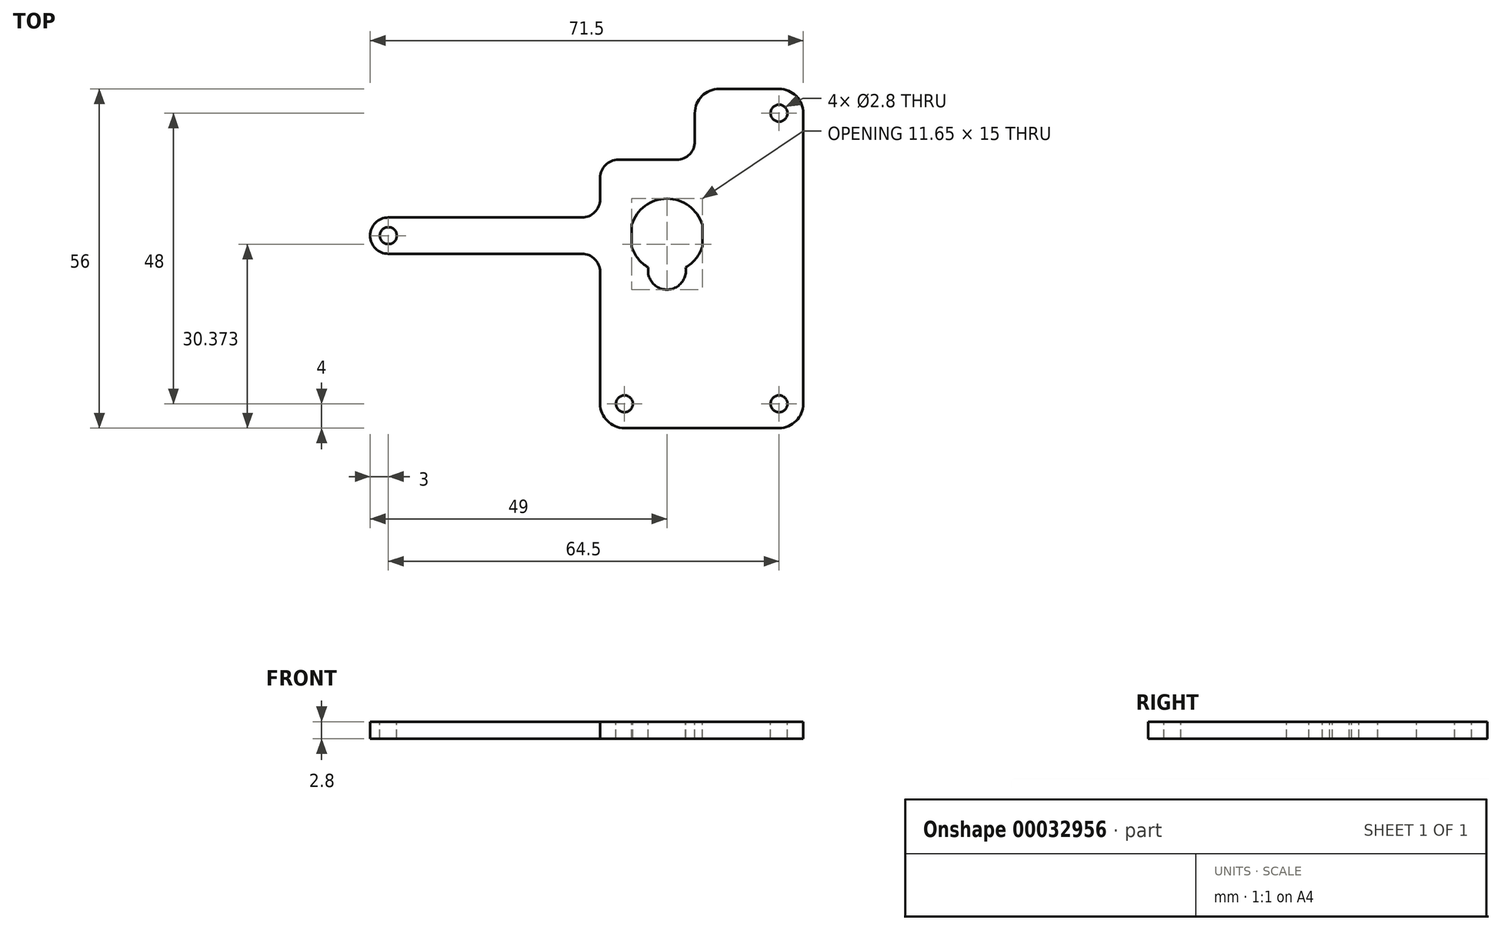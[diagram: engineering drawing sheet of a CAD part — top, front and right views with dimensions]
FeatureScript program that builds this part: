
annotation { "Feature Type Name" : "Feature", "Feature Type Description" : "" }
export const myFeature = defineFeature(function(context is Context, id is Id, definition is map)
    precondition{}
    {
        {
            var Q0;
            Q0=qCreatedBy(makeId("Top.planeOp"),FACE);
            var sketch = newSketch(context, id + "F0", { "sketchPlane" : qUnion([Q0])});
            skLineSegment(sketch, "E0.rect.bottom", {"start": v(5.82, -11.88) * mm, "end": v(-5.83, -11.88) * mm});
            skLineSegment(sketch, "E0.rect.top", {"start": v(5.83, 11.88) * mm, "end": v(-5.82, 11.88) * mm});
            skLineSegment(sketch, "E0.rect.left", {"start": v(5.82, -11.88) * mm, "end": v(5.83, 11.88) * mm});
            skLineSegment(sketch, "E0.rect.right", {"start": v(-5.83, -11.88) * mm, "end": v(-5.82, 11.87) * mm});
            skPoint(sketch, "E0.rect.middle", {"position": v(0, 0) * mm});
            skSolve(sketch);
        }
        {
            var Q0;
            Q0=qSketchRegion(id+"F0",true);
            extrude(context, id + "F1", {"entities" : qUnion([Q0]), "depth" : 20.4 * mm});
        }
        {
            var Q0;
            Q0=makeQuery(id+"F1.opExtrude","CAP_FACE",FACE,{"disambiguationData":[OSD([sQuery(id+"F0.wireOp",EDGE,"E0.rect.bottom"),sQuery(id+"F0.wireOp",EDGE,"E0.rect.top"),sQuery(id+"F0.wireOp",EDGE,"E0.rect.left"),sQuery(id+"F0.wireOp",EDGE,"E0.rect.right")])],"isStart":false});
            var sketch = newSketch(context, id + "F2", { "sketchPlane" : qUnion([Q0])});
            skArc(sketch, "E1", {"start": v(5.83, 7.59) * mm, "mid": v(0, 11.88) * mm, "end": v(-5.83, 7.59) * mm});
            skLineSegment(sketch, "E2", {"start": v(5.83, 7.59) * mm, "end": v(5.83, 3.96) * mm});
            skLineSegment(sketch, "E3.MirrorCS", {"start": v(-5.83, 7.59) * mm, "end": v(-5.83, 3.96) * mm});
            skArc(sketch, "E4.trimOffspring", {"start": v(-5.83, 3.96) * mm, "mid": v(-4.78, 1.98) * mm, "end": v(-3.09, 0.51) * mm});
            skArc(sketch, "E5", {"start": v(-3.09, 0.51) * mm, "mid": v(0, -3.1) * mm, "end": v(3.09, 0.51) * mm});
            skArc(sketch, "E6.trimOffspring", {"start": v(3.09, 0.51) * mm, "mid": v(4.78, 1.98) * mm, "end": v(5.83, 3.96) * mm});
            skSolve(sketch);
        }
        {
            var Q0;
            Q0=qSketchRegion(id+"F2",true);
            extrude(context, id + "F3", {"entities" : qUnion([Q0]), "operationType" : NewBodyOperationType.ADD, "depth" : 6 * mm});
        }
        {
            var Q0;
            {var subQ0=sQuery(id+"F0.wireOp",EDGE,"E0.rect.bottom");var subQ1=sQuery(id+"F0.wireOp",EDGE,"E0.rect.left");var subQ2=sQuery(id+"F0.wireOp",EDGE,"E0.rect.right");Q0=makeQuery(id+"F3.boolean.opBoolean","SPLIT",FACE,{"disambiguationData":[TD([makeQuery(id+"F1.opExtrude","SWEPT_FACE",FACE,{"disambiguationData":[OSD([subQ0])]}),makeQuery(id+"F1.opExtrude","SWEPT_FACE",FACE,{"disambiguationData":[OSD([subQ1])]}),makeQuery(id+"F1.opExtrude","SWEPT_FACE",FACE,{"disambiguationData":[OSD([subQ2])]}),makeQuery(id+"F3.opExtrude","SWEPT_FACE",FACE,{"disambiguationData":[OSD([sQuery(id+"F2.wireOp",EDGE,"E2")])]}),makeQuery(id+"F3.opExtrude","SWEPT_FACE",FACE,{"disambiguationData":[OSD([sQuery(id+"F2.wireOp",EDGE,"E3.MirrorCS")])]}),makeQuery(id+"F3.opExtrude","SWEPT_FACE",FACE,{"disambiguationData":[OSD([sQuery(id+"F2.wireOp",EDGE,"E4.trimOffspring")])]}),makeQuery(id+"F3.opExtrude","SWEPT_FACE",FACE,{"disambiguationData":[OSD([sQuery(id+"F2.wireOp",EDGE,"E5")])]}),makeQuery(id+"F3.opExtrude","SWEPT_FACE",FACE,{"disambiguationData":[OSD([sQuery(id+"F2.wireOp",EDGE,"E6.trimOffspring")])]})])],"derivedFrom":makeQuery(id+"F1.opExtrude","CAP_FACE",FACE,{"disambiguationData":[OSD([subQ0,sQuery(id+"F0.wireOp",EDGE,"E0.rect.top"),subQ1,subQ2])],"isStart":false})});}
            var sketch = newSketch(context, id + "F4", { "sketchPlane" : qUnion([Q0])});
            skLineSegment(sketch, "E7.bottom", {"start": v(-5.83, -11.88) * mm, "end": v(5.82, -11.88) * mm});
            skLineSegment(sketch, "E7.top", {"start": v(-5.83, -16.08) * mm, "end": v(5.82, -16.08) * mm});
            skLineSegment(sketch, "E7.left", {"start": v(-5.83, -11.88) * mm, "end": v(-5.83, -16.08) * mm});
            skLineSegment(sketch, "E7.right", {"start": v(5.82, -11.88) * mm, "end": v(5.82, -16.08) * mm});
            skLineSegment(sketch, "E8.MirrorCS", {"start": v(-5.83, 11.88) * mm, "end": v(-5.83, 16.08) * mm});
            skLineSegment(sketch, "E9.MirrorCS", {"start": v(-5.83, 16.08) * mm, "end": v(5.82, 16.08) * mm});
            skLineSegment(sketch, "E10.MirrorCS", {"start": v(5.82, 11.88) * mm, "end": v(5.82, 16.08) * mm});
            skLineSegment(sketch, "E11.MirrorCS", {"start": v(-5.83, 11.88) * mm, "end": v(5.82, 11.88) * mm});
            skSolve(sketch);
        }
        {
            var Q0;
            Q0=makeQuery(id+"F4.imprint","IMPRINT",FACE,{"disambiguationData":[TD([[makeQuery(id+"F4.imprint","IMPRINT",EDGE,{"derivedFrom":sQuery(id+"F4.wireOp",EDGE,"E7.bottom")}),1.0]])]});
            var Q1;
            Q1=makeQuery(id+"F4.imprint","IMPRINT",FACE,{"disambiguationData":[TD([[makeQuery(id+"F4.imprint","IMPRINT",EDGE,{"derivedFrom":sQuery(id+"F4.wireOp",EDGE,"E8.MirrorCS")}),-1.0]])]});
            extrude(context, id + "F5", {"entities" : qUnion([Q0, Q1]), "operationType" : NewBodyOperationType.ADD, "oppositeDirection" : true, "depth" : 2.8 * mm, "hasSecondDirection" : true, "secondDirectionOppositeDirection" : true, "secondDirectionDepth" : .8 * mm});
        }
        {
            var Q0;
            {var subQ0=sQuery(id+"F0.wireOp",EDGE,"E0.rect.top");var subQ1=sQuery(id+"F0.wireOp",EDGE,"E0.rect.left");Q0=makeQuery(id+"F5.boolean.opBoolean","SPLIT",EDGE,{"disambiguationData":[TD([makeQuery(id+"F1.opExtrude","CAP_FACE",FACE,{"disambiguationData":[OSD([sQuery(id+"F0.wireOp",EDGE,"E0.rect.bottom"),subQ0,subQ1,sQuery(id+"F0.wireOp",EDGE,"E0.rect.right")])],"isStart":true})])],"derivedFrom":makeQuery(id+"F1.opExtrude","SWEPT_EDGE",EDGE,{"disambiguationData":[OSD([subQ0,subQ1])]})});}
            var Q1;
            {var subQ0=sQuery(id+"F0.wireOp",EDGE,"E0.rect.bottom");var subQ1=sQuery(id+"F0.wireOp",EDGE,"E0.rect.left");Q1=makeQuery(id+"F5.boolean.opBoolean","SPLIT",EDGE,{"disambiguationData":[TD([makeQuery(id+"F1.opExtrude","CAP_FACE",FACE,{"disambiguationData":[OSD([subQ0,sQuery(id+"F0.wireOp",EDGE,"E0.rect.top"),subQ1,sQuery(id+"F0.wireOp",EDGE,"E0.rect.right")])],"isStart":true})])],"derivedFrom":makeQuery(id+"F1.opExtrude","SWEPT_EDGE",EDGE,{"disambiguationData":[OSD([subQ0,subQ1])]})});}
            var Q2;
            {var subQ0=sQuery(id+"F0.wireOp",EDGE,"E0.rect.bottom");var subQ1=sQuery(id+"F0.wireOp",EDGE,"E0.rect.right");Q2=makeQuery(id+"F5.boolean.opBoolean","SPLIT",EDGE,{"disambiguationData":[TD([makeQuery(id+"F1.opExtrude","CAP_FACE",FACE,{"disambiguationData":[OSD([subQ0,sQuery(id+"F0.wireOp",EDGE,"E0.rect.top"),sQuery(id+"F0.wireOp",EDGE,"E0.rect.left"),subQ1])],"isStart":true})])],"derivedFrom":makeQuery(id+"F1.opExtrude","SWEPT_EDGE",EDGE,{"disambiguationData":[OSD([subQ0,subQ1])]})});}
            var Q3;
            {var subQ0=sQuery(id+"F0.wireOp",EDGE,"E0.rect.top");var subQ1=sQuery(id+"F0.wireOp",EDGE,"E0.rect.right");Q3=makeQuery(id+"F5.boolean.opBoolean","SPLIT",EDGE,{"disambiguationData":[TD([makeQuery(id+"F1.opExtrude","CAP_FACE",FACE,{"disambiguationData":[OSD([sQuery(id+"F0.wireOp",EDGE,"E0.rect.bottom"),subQ0,sQuery(id+"F0.wireOp",EDGE,"E0.rect.left"),subQ1])],"isStart":true})])],"derivedFrom":makeQuery(id+"F1.opExtrude","SWEPT_EDGE",EDGE,{"disambiguationData":[OSD([subQ0,subQ1])]})});}
            fillet(context, id + "F6", {"entities" : qUnion([Q0, Q1, Q2, Q3]), "radius" : .5 * mm, "tangentPropagation" : true, "allowEdgeOverflow" : false});
        }
        {
            var Q0;
            Q0=makeQuery(id+"F5.opExtrude","SWEPT_EDGE",EDGE,{"disambiguationData":[OSD([sQuery(id+"F4.wireOp",EDGE,"E8.MirrorCS"),sQuery(id+"F4.wireOp",EDGE,"E9.MirrorCS")])]});
            var Q1;
            Q1=makeQuery(id+"F5.opExtrude","SWEPT_EDGE",EDGE,{"disambiguationData":[OSD([sQuery(id+"F4.wireOp",EDGE,"E9.MirrorCS"),sQuery(id+"F4.wireOp",EDGE,"E10.MirrorCS")])]});
            var Q2;
            Q2=makeQuery(id+"F5.opExtrude","SWEPT_EDGE",EDGE,{"disambiguationData":[OSD([sQuery(id+"F4.wireOp",EDGE,"E7.top"),sQuery(id+"F4.wireOp",EDGE,"E7.right")])]});
            var Q3;
            Q3=makeQuery(id+"F5.opExtrude","SWEPT_EDGE",EDGE,{"disambiguationData":[OSD([sQuery(id+"F4.wireOp",EDGE,"E7.top"),sQuery(id+"F4.wireOp",EDGE,"E7.left")])]});
            fillet(context, id + "F7", {"entities" : qUnion([Q0, Q1, Q2, Q3]), "radius" : 1 * mm, "tangentPropagation" : true, "allowEdgeOverflow" : false});
        }
        {
            var Q0;
            Q0=makeQuery(id+"F3.opExtrude","CAP_FACE",FACE,{"disambiguationData":[OSD([sQuery(id+"F2.wireOp",EDGE,"E1"),sQuery(id+"F2.wireOp",EDGE,"E2"),sQuery(id+"F2.wireOp",EDGE,"E3.MirrorCS"),sQuery(id+"F2.wireOp",EDGE,"E4.trimOffspring"),sQuery(id+"F2.wireOp",EDGE,"E5"),sQuery(id+"F2.wireOp",EDGE,"E6.trimOffspring")])],"isStart":false});
            var sketch = newSketch(context, id + "F8", { "sketchPlane" : qUnion([Q0])});
            skArc(sketch, "E12", {"start": v(3.09, 0.51) * mm, "mid": v(4.78, 1.98) * mm, "end": v(5.83, 3.96) * mm});
            skArc(sketch, "E13", {"start": v(-3.09, 0.51) * mm, "mid": v(0, -3.13) * mm, "end": v(3.09, 0.51) * mm});
            skLineSegment(sketch, "E14", {"start": v(-5.83, 3.96) * mm, "end": v(-5.83, 7.59) * mm});
            skLineSegment(sketch, "E15.MirrorCS", {"start": v(5.83, 3.96) * mm, "end": v(5.83, 7.59) * mm});
            skArc(sketch, "E16.trimOffspring", {"start": v(-5.83, 3.96) * mm, "mid": v(-4.78, 1.98) * mm, "end": v(-3.09, 0.51) * mm});
            skArc(sketch, "E17.trimOffspring", {"start": v(5.83, 7.59) * mm, "mid": v(0, 11.88) * mm, "end": v(-5.83, 7.59) * mm});
            skLineSegment(sketch, "E18.rect.bottom", {"start": v(22.5, 30) * mm, "end": v(4.61, 30) * mm});
            skLineSegment(sketch, "E18.rect.left", {"start": v(22.5, 30) * mm, "end": v(22.5, -26) * mm});
            skCircle(sketch, "E19.MirrorC", {"center": v(18.5, 26) * mm, "radius": 1.4 * mm});
            skLineSegment(sketch, "E20", {"start": v(4.61, 30) * mm, "end": v(4.61, 21.32) * mm});
            skLineSegment(sketch, "E21", {"start": v(1.61, 18.32) * mm, "end": v(-8.03, 18.32) * mm});
            skLineSegment(sketch, "E22", {"start": v(-11.03, 15.32) * mm, "end": v(-11.03, 11.78) * mm});
            skPoint(sketch, "E23.orphan", {"position": v(-22.5, 30) * mm});
            skPoint(sketch, "E24.visualSharp", {"position": v(-11.03, -26) * mm});
            skPoint(sketch, "E25.visualSharp", {"position": v(4.61, 18.32) * mm});
            skArc(sketch, "E25.filletArc", {"start": v(1.61, 18.32) * mm, "mid": v(3.73, 19.2) * mm, "end": v(4.61, 21.32) * mm});
            skPoint(sketch, "E26.visualSharp", {"position": v(-11.03, 18.32) * mm});
            skArc(sketch, "E26.filletArc", {"start": v(-8.03, 18.32) * mm, "mid": v(-10.15, 17.44) * mm, "end": v(-11.03, 15.32) * mm});
            skLineSegment(sketch, "E27", {"start": v(0, 5.78) * mm, "end": v(-46, 5.78) * mm, "construction": true});
            skCircle(sketch, "E28", {"center": v(-46, 5.78) * mm, "radius": 1.4 * mm});
            skArc(sketch, "E29", {"start": v(-46, 8.78) * mm, "mid": v(-49, 5.78) * mm, "end": v(-46, 2.78) * mm});
            skLineSegment(sketch, "E30", {"start": v(-46, 2.78) * mm, "end": v(-14.03, 2.78) * mm});
            skLineSegment(sketch, "E31.MirrorCS", {"start": v(-46, 8.78) * mm, "end": v(-14.03, 8.78) * mm});
            skLineSegment(sketch, "E32.trimOffspring", {"start": v(-11.03, -0.22) * mm, "end": v(-11.03, -15.07) * mm});
            skPoint(sketch, "E33.visualSharp", {"position": v(-11.03, 8.78) * mm});
            skArc(sketch, "E33.filletArc", {"start": v(-14.03, 8.78) * mm, "mid": v(-11.9, 9.65) * mm, "end": v(-11.03, 11.78) * mm});
            skPoint(sketch, "E34.visualSharp", {"position": v(-11.03, 2.78) * mm});
            skArc(sketch, "E34.filletArc", {"start": v(-11.03, -0.22) * mm, "mid": v(-11.9, 1.9) * mm, "end": v(-14.03, 2.77) * mm});
            skLineSegment(sketch, "E35", {"start": v(-11.03, -15.07) * mm, "end": v(-11.03, -26) * mm});
            skLineSegment(sketch, "E36", {"start": v(-11.03, -26) * mm, "end": v(22.5, -26) * mm});
            skLineSegment(sketch, "E37.bottom", {"start": v(-11.03, -26) * mm, "end": v(-7.03, -26) * mm, "construction": true});
            skLineSegment(sketch, "E37.top", {"start": v(-11.03, -22) * mm, "end": v(-7.03, -22) * mm, "construction": true});
            skLineSegment(sketch, "E37.left", {"start": v(-11.03, -26) * mm, "end": v(-11.03, -22) * mm, "construction": true});
            skLineSegment(sketch, "E37.right", {"start": v(-7.03, -26) * mm, "end": v(-7.03, -22) * mm, "construction": true});
            skCircle(sketch, "E38", {"center": v(-7.03, -22) * mm, "radius": 1.4 * mm});
            skLineSegment(sketch, "E39.bottom", {"start": v(22.5, -26) * mm, "end": v(18.5, -26) * mm, "construction": true});
            skLineSegment(sketch, "E39.top", {"start": v(22.5, -22) * mm, "end": v(18.5, -22) * mm, "construction": true});
            skLineSegment(sketch, "E39.left", {"start": v(22.5, -26) * mm, "end": v(22.5, -22) * mm, "construction": true});
            skLineSegment(sketch, "E39.right", {"start": v(18.5, -26) * mm, "end": v(18.5, -22) * mm, "construction": true});
            skCircle(sketch, "E40", {"center": v(18.5, -22) * mm, "radius": 1.4 * mm});
            skSolve(sketch);
        }
        {
            var Q0;
            Q0=qSketchRegion(id+"F8",true);
            extrude(context, id + "F9", {"entities" : qUnion([Q0]), "oppositeDirection" : true, "depth" : 2.8 * mm});
        }
        {
            var Q0;
            Q0=makeQuery(id+"F9.opExtrude","SWEPT_EDGE",EDGE,{"disambiguationData":[OSD([sQuery(id+"F8.wireOp",EDGE,"E18.rect.top"),sQuery(id+"F8.wireOp",EDGE,"E18.rect.right")])]});
            var Q1;
            Q1=makeQuery(id+"F9.opExtrude","SWEPT_EDGE",EDGE,{"disambiguationData":[OSD([sQuery(id+"F8.wireOp",EDGE,"E18.rect.bottom"),sQuery(id+"F8.wireOp",EDGE,"E18.rect.right")])]});
            var Q2;
            Q2=makeQuery(id+"F9.opExtrude","SWEPT_EDGE",EDGE,{"disambiguationData":[OSD([sQuery(id+"F8.wireOp",EDGE,"E18.rect.bottom"),sQuery(id+"F8.wireOp",EDGE,"E18.rect.left")])]});
            var Q3;
            Q3=makeQuery(id+"F9.opExtrude","SWEPT_EDGE",EDGE,{"disambiguationData":[OSD([sQuery(id+"F8.wireOp",EDGE,"E18.rect.top"),sQuery(id+"F8.wireOp",EDGE,"E18.rect.left")])]});
            var Q4;
            Q4=makeQuery(id+"F9.opExtrude","SWEPT_EDGE",EDGE,{"disambiguationData":[OSD([sQuery(id+"F8.wireOp",EDGE,"E35"),sQuery(id+"F8.wireOp",EDGE,"E36")])]});
            fillet(context, id + "F10", {"entities" : qUnion([Q0, Q1, Q2, Q3, Q4]), "radius" : 4 * mm, "tangentPropagation" : true, "allowEdgeOverflow" : false});
        }
        {
            var Q0;
            Q0=makeQuery(id+"F9.opExtrude","SWEPT_BODY",BODY,{"disambiguationData":[OSD([sQuery(id+"F8.wireOp",EDGE,"E12"),sQuery(id+"F8.wireOp",EDGE,"E13"),sQuery(id+"F8.wireOp",EDGE,"E14"),sQuery(id+"F8.wireOp",EDGE,"E15.MirrorCS"),sQuery(id+"F8.wireOp",EDGE,"E16.trimOffspring"),sQuery(id+"F8.wireOp",EDGE,"E17.trimOffspring"),sQuery(id+"F8.wireOp",EDGE,"E18.rect.bottom"),sQuery(id+"F8.wireOp",EDGE,"E18.rect.top"),sQuery(id+"F8.wireOp",EDGE,"E18.rect.left"),sQuery(id+"F8.wireOp",EDGE,"E18.rect.right"),sQuery(id+"F8.wireOp",EDGE,"a12ce330-09d9-461c-8b2f-e163017ed208"),sQuery(id+"F8.wireOp",EDGE,"ce85554a-ae08-408d-bbdd-004999f886530.MirrorC"),sQuery(id+"F8.wireOp",EDGE,"74581e88-93ef-4e49-bf24-ccc966527bf30.MirrorC"),sQuery(id+"F8.wireOp",EDGE,"E19.MirrorC"),sQuery(id+"F8.wireOp",EDGE,"76930b9b-8da1-4d4d-b0e5-4a7641f42912"),sQuery(id+"F8.wireOp",EDGE,"f42893a9-d5a1-4c2e-96db-01520e8eb7290.MirrorC"),sQuery(id+"F8.wireOp",EDGE,"46118b25-6d7d-4224-8583-2d73bb83e9220.MirrorC"),sQuery(id+"F8.wireOp",EDGE,"b2e64fab-b84c-4731-9833-593c73ce0a330.MirrorC")])]});
            transform(context, id + "F11", {"entities" : qUnion([Q0]), "transformType" : TransformType.TRANSLATION_3D, "dx" : 0 * mm, "dy" : 0 * mm, "dz" : 0 * mm, "makeCopy" : true});
        }
        {
            var Q0;
            Q0=makeQuery(id+"F11.opPattern","COPY",BODY,{"derivedFrom":makeQuery(id+"F9.opExtrude","SWEPT_BODY",BODY,{"disambiguationData":[OSD([sQuery(id+"F8.wireOp",EDGE,"E12"),sQuery(id+"F8.wireOp",EDGE,"E13"),sQuery(id+"F8.wireOp",EDGE,"E14"),sQuery(id+"F8.wireOp",EDGE,"E15.MirrorCS"),sQuery(id+"F8.wireOp",EDGE,"E16.trimOffspring"),sQuery(id+"F8.wireOp",EDGE,"E17.trimOffspring"),sQuery(id+"F8.wireOp",EDGE,"E18.rect.bottom"),sQuery(id+"F8.wireOp",EDGE,"E18.rect.top"),sQuery(id+"F8.wireOp",EDGE,"E18.rect.left"),sQuery(id+"F8.wireOp",EDGE,"E18.rect.right"),sQuery(id+"F8.wireOp",EDGE,"a12ce330-09d9-461c-8b2f-e163017ed208"),sQuery(id+"F8.wireOp",EDGE,"74581e88-93ef-4e49-bf24-ccc966527bf30.MirrorC"),sQuery(id+"F8.wireOp",EDGE,"E19.MirrorC"),sQuery(id+"F8.wireOp",EDGE,"76930b9b-8da1-4d4d-b0e5-4a7641f42912"),sQuery(id+"F8.wireOp",EDGE,"f42893a9-d5a1-4c2e-96db-01520e8eb7290.MirrorC"),sQuery(id+"F8.wireOp",EDGE,"b2e64fab-b84c-4731-9833-593c73ce0a330.MirrorC"),sQuery(id+"F8.wireOp",EDGE,"E20"),sQuery(id+"F8.wireOp",EDGE,"E21"),sQuery(id+"F8.wireOp",EDGE,"E22"),sQuery(id+"F8.wireOp",EDGE,"8f80475a-625c-4095-acb9-1eab8cfb7864"),sQuery(id+"F8.wireOp",EDGE,"E24.filletArc"),sQuery(id+"F8.wireOp",EDGE,"E25.filletArc"),sQuery(id+"F8.wireOp",EDGE,"E26.filletArc")])]}),"instanceName":"1"});
            deleteBodies(context, id + "F12", {"entities" : qUnion([Q0])});
        }
        {
            var Q0;
            Q0=makeQuery(id+"F1.opExtrude","SWEPT_BODY",BODY,{"disambiguationData":[OSD([sQuery(id+"F0.wireOp",EDGE,"E0.rect.bottom"),sQuery(id+"F0.wireOp",EDGE,"E0.rect.top"),sQuery(id+"F0.wireOp",EDGE,"E0.rect.left"),sQuery(id+"F0.wireOp",EDGE,"E0.rect.right")])]});
            deleteBodies(context, id + "F13", {"entities" : qUnion([Q0])});
        }
    });
